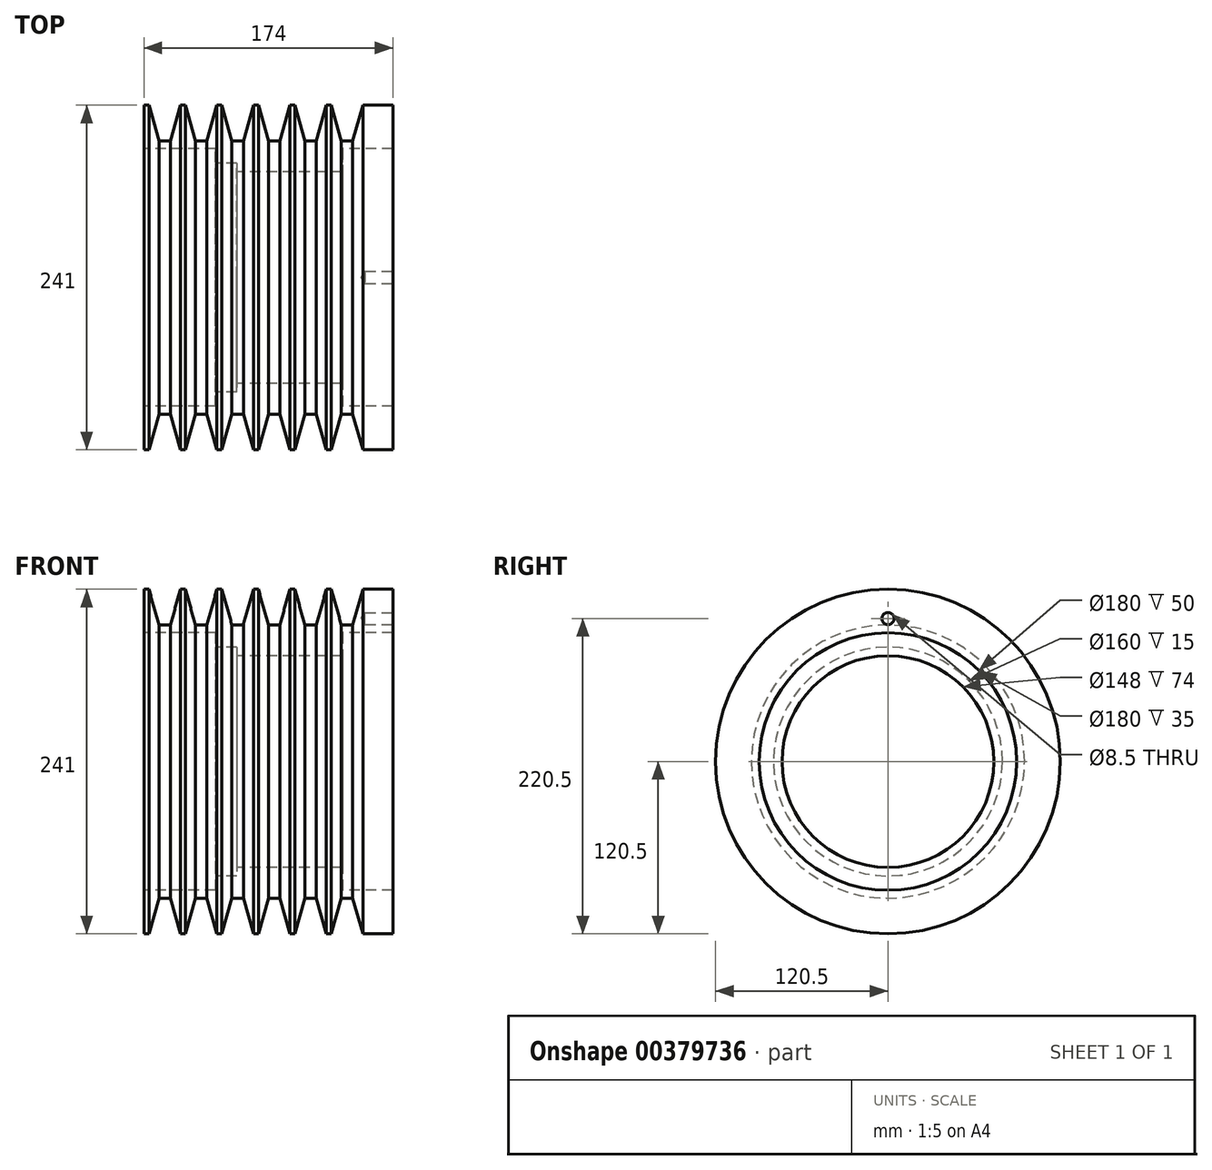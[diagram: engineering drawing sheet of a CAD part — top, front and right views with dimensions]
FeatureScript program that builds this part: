
annotation { "Feature Type Name" : "Feature", "Feature Type Description" : "" }
export const myFeature = defineFeature(function(context is Context, id is Id, definition is map)
    precondition{}
    {
        {
            var Q0;
            Q0=qCreatedBy(makeId("Front.planeOp"),FACE);
            var sketch = newSketch(context, id + "F0", { "sketchPlane" : qUnion([Q0])});
            skLineSegment(sketch, "E0.right", {"start": v(-87, 14) * mm, "end": v(-87, -16.5) * mm});
            skLineSegment(sketch, "E1", {"start": v(87, 14) * mm, "end": v(87, -16.5) * mm});
            skLineSegment(sketch, "E2", {"start": v(-87, 14) * mm, "end": v(-83.5, 14) * mm});
            skLineSegment(sketch, "E3", {"start": v(-61.5, 14) * mm, "end": v(-58, 14) * mm});
            skLineSegment(sketch, "E4", {"start": v(-36, 14) * mm, "end": v(-32.5, 14) * mm});
            skLineSegment(sketch, "E5", {"start": v(-10.5, 14) * mm, "end": v(-7, 14) * mm});
            skLineSegment(sketch, "E6", {"start": v(15, 14) * mm, "end": v(18.5, 14) * mm});
            skLineSegment(sketch, "E7", {"start": v(40.5, 14) * mm, "end": v(44, 14) * mm});
            skLineSegment(sketch, "E8", {"start": v(66, 14) * mm, "end": v(87, 14) * mm});
            skLineSegment(sketch, "E9", {"start": v(-68.5, -11) * mm, "end": v(-61.5, 14) * mm});
            skLineSegment(sketch, "E10", {"start": v(-68.5, -11) * mm, "end": v(-76.5, -11) * mm});
            skLineSegment(sketch, "E11", {"start": v(-76.5, -11) * mm, "end": v(-83.5, 14) * mm});
            skLineSegment(sketch, "E12", {"start": v(-43, -11) * mm, "end": v(-36, 14) * mm});
            skLineSegment(sketch, "E13", {"start": v(-43, -11) * mm, "end": v(-51, -11) * mm});
            skLineSegment(sketch, "E14", {"start": v(-51, -11) * mm, "end": v(-58, 14) * mm});
            skLineSegment(sketch, "E15", {"start": v(-17.5, -11) * mm, "end": v(-10.5, 14) * mm});
            skLineSegment(sketch, "E16", {"start": v(-17.5, -11) * mm, "end": v(-25.5, -11) * mm});
            skLineSegment(sketch, "E17", {"start": v(-25.5, -11) * mm, "end": v(-32.5, 14) * mm});
            skLineSegment(sketch, "E18", {"start": v(8, -11) * mm, "end": v(15, 14) * mm});
            skLineSegment(sketch, "E19", {"start": v(8, -11) * mm, "end": v(0, -11) * mm});
            skLineSegment(sketch, "E20", {"start": v(0, -11) * mm, "end": v(-7, 14) * mm});
            skLineSegment(sketch, "E21", {"start": v(33.5, -11) * mm, "end": v(40.5, 14) * mm});
            skLineSegment(sketch, "E22", {"start": v(33.5, -11) * mm, "end": v(25.5, -11) * mm});
            skLineSegment(sketch, "E23", {"start": v(25.5, -11) * mm, "end": v(18.5, 14) * mm});
            skLineSegment(sketch, "E24", {"start": v(59, -11) * mm, "end": v(66, 14) * mm});
            skLineSegment(sketch, "E25", {"start": v(59, -11) * mm, "end": v(51, -11) * mm});
            skLineSegment(sketch, "E26", {"start": v(51, -11) * mm, "end": v(44, 14) * mm});
            skLineSegment(sketch, "E27", {"start": v(-104.1, -106.5) * mm, "end": v(121.89, -106.5) * mm, "construction": true});
            skLineSegment(sketch, "E28", {"start": v(87, -16.5) * mm, "end": v(52, -16.5) * mm});
            skLineSegment(sketch, "E29", {"start": v(-87, -16.5) * mm, "end": v(-37, -16.5) * mm});
            skLineSegment(sketch, "E30", {"start": v(-37, -16.5) * mm, "end": v(-37, -26.5) * mm});
            skLineSegment(sketch, "E31", {"start": v(-37, -26.5) * mm, "end": v(-22, -26.5) * mm});
            skLineSegment(sketch, "E32", {"start": v(-22, -26.5) * mm, "end": v(-22, -32.5) * mm});
            skLineSegment(sketch, "E33", {"start": v(-22, -32.5) * mm, "end": v(52, -32.5) * mm});
            skLineSegment(sketch, "E34", {"start": v(52, -32.5) * mm, "end": v(52, -16.5) * mm});
            skLineSegment(sketch, "E35", {"start": v(-72.5, -11) * mm, "end": v(-72.5, 36.92) * mm, "construction": true});
            skLineSegment(sketch, "E36", {"start": v(-47, -11) * mm, "end": v(-47, 36.92) * mm, "construction": true});
            skLineSegment(sketch, "E37", {"start": v(55, -11) * mm, "end": v(55, 36.92) * mm, "construction": true});
            skSolve(sketch);
        }
        {
            var Q0;
            Q0=makeQuery(id+"F0.imprint","IMPRINT",FACE,{"disambiguationData":[TD([[makeQuery(id+"F0.imprint","IMPRINT",EDGE,{"derivedFrom":sQuery(id+"F0.wireOp",EDGE,"E0.top")}),-1.0]])]});
            var Q1;
            Q1=makeQuery(id+"F0.imprint","IMPRINT",FACE,{"disambiguationData":[TD([[makeQuery(id+"F0.imprint","IMPRINT",EDGE,{"derivedFrom":sQuery(id+"F0.wireOp",EDGE,"E0.right")}),1.0]])]});
            var Q2;
            Q2=sQuery(id+"F0.wireOp",EDGE,"E27");
            var Q3;
            Q3=sQuery(id+"F0.wireOp",EDGE,"E27");
            revolve(context, id + "F1", {"entities" : qUnion([Q0, Q1]), "surfaceEntities" : qUnion([Q2]), "axis" : qUnion([Q3]), "revolveType" : RevolveType.FULL});
        }
        {
            var Q0;
            Q0=makeQuery(id+"F1.opRevolve","SWEPT_FACE",FACE,{"disambiguationData":[OSD([sQuery(id+"F0.wireOp",EDGE,"E1")])]});
            var sketch = newSketch(context, id + "F2", { "sketchPlane" : qUnion([Q0])});
            skCircle(sketch, "E38", {"center": v(0, -106.5) * mm, "radius": 100 * mm});
            skLineSegment(sketch, "E39", {"start": v(0, -6.5) * mm, "end": v(-28.36, -6.5) * mm});
            skCircle(sketch, "E40", {"center": v(0, -6.5) * mm, "radius": 4.5 * mm});
            skSolve(sketch);
        }
        {
            var Q0;
            Q0=sQuery(id+"F2.wireOp",VERTEX,"E40.center");
            var Q1;
            Q1=makeQuery(id+"F1.opRevolve","SWEPT_BODY",BODY,{"disambiguationData":[OSD([sQuery(id+"F0.wireOp",EDGE,"E0.right"),sQuery(id+"F0.wireOp",EDGE,"E1"),sQuery(id+"F0.wireOp",EDGE,"E2"),sQuery(id+"F0.wireOp",EDGE,"E3"),sQuery(id+"F0.wireOp",EDGE,"E4"),sQuery(id+"F0.wireOp",EDGE,"E5"),sQuery(id+"F0.wireOp",EDGE,"E6"),sQuery(id+"F0.wireOp",EDGE,"E7"),sQuery(id+"F0.wireOp",EDGE,"E8"),sQuery(id+"F0.wireOp",EDGE,"E9"),sQuery(id+"F0.wireOp",EDGE,"E10"),sQuery(id+"F0.wireOp",EDGE,"E11"),sQuery(id+"F0.wireOp",EDGE,"E12"),sQuery(id+"F0.wireOp",EDGE,"E13"),sQuery(id+"F0.wireOp",EDGE,"E14"),sQuery(id+"F0.wireOp",EDGE,"E15"),sQuery(id+"F0.wireOp",EDGE,"E16"),sQuery(id+"F0.wireOp",EDGE,"E17"),sQuery(id+"F0.wireOp",EDGE,"E18"),sQuery(id+"F0.wireOp",EDGE,"E19"),sQuery(id+"F0.wireOp",EDGE,"E20"),sQuery(id+"F0.wireOp",EDGE,"E21"),sQuery(id+"F0.wireOp",EDGE,"E22"),sQuery(id+"F0.wireOp",EDGE,"E23"),sQuery(id+"F0.wireOp",EDGE,"E24"),sQuery(id+"F0.wireOp",EDGE,"E25"),sQuery(id+"F0.wireOp",EDGE,"E26"),sQuery(id+"F0.wireOp",EDGE,"E28"),sQuery(id+"F0.wireOp",EDGE,"E29"),sQuery(id+"F0.wireOp",EDGE,"E30"),sQuery(id+"F0.wireOp",EDGE,"E31"),sQuery(id+"F0.wireOp",EDGE,"E32"),sQuery(id+"F0.wireOp",EDGE,"E33"),sQuery(id+"F0.wireOp",EDGE,"E34")])]});
            hole(context, id + "F3", {"style" : HoleStyle.SIMPLE, "endStyle" : HoleEndStyle.BLIND, "standardTappedOrClearance" : lookupTablePath({ "standard" : "ISO", "engagement" : "75%", "pitch" : "1.5 mm", "size" : "M10", "type" : "Tapped" }), "standardBlindInLast" : lookupTablePath({ "standard" : "ISO", "engagement" : "75%", "pitch" : "1.5 mm", "size" : "M10", "type" : "Tapped" }), "holeDiameter" : 8.5 * mm, "showTappedDepth" : true, "holeDepth" : 19.5 * mm, "isTappedThrough" : true, "tappedDepth" : 15 * mm, "tapClearance" : 3, "locations" : qUnion([Q0]), "scope" : qUnion([Q1]), "majorDiameter" : 10 * mm});
        }
    });
